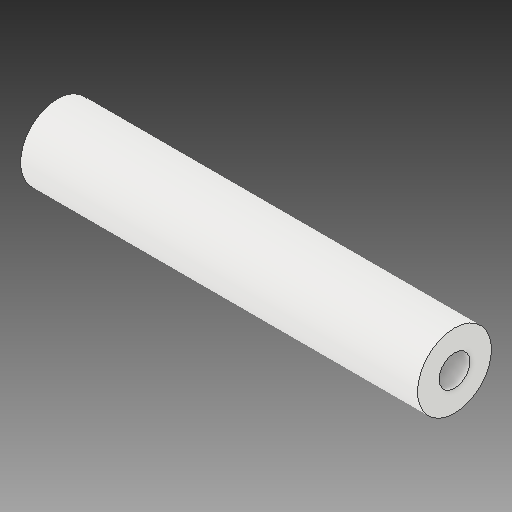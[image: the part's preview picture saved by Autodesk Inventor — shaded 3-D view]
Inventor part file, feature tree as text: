
AUTODESK INVENTOR PART (.ipt)
format: ipt  version: 2019 (Build 230136000, 136)  size: 102,912 bytes
history: native  units: mm
features: extrude x1, sketch x1
ambient origin geometry x8: Origin, YZ Plane, XZ Plane, XY Plane, X Axis, Y Axis, Z Axis, Center Point
bodies: Solid1 (feature_tree)
feature tree (2):
  extrude  "Extrusion1"  Depth=64.439mm
  sketch  "Sketch1"  dims[d1=12.0mm d2=5.0mm d3=64.439mm d4=0.0mm]
